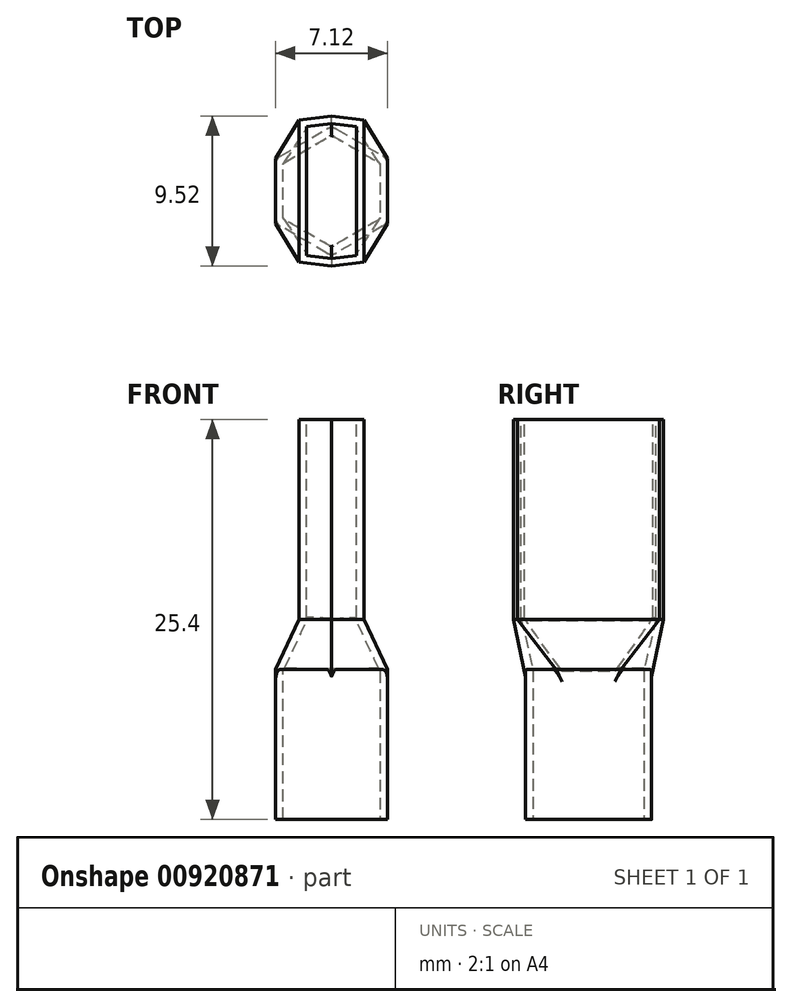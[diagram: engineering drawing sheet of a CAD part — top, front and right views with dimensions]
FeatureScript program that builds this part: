
annotation { "Feature Type Name" : "Feature", "Feature Type Description" : "" }
export const myFeature = defineFeature(function(context is Context, id is Id, definition is map)
    precondition{}
    {
        {
            var Q0;
            Q0=qCreatedBy(makeId("Top.planeOp"),FACE);
            var sketch = newSketch(context, id + "F0", { "sketchPlane" : qUnion([Q0])});
            skCircle(sketch, "E0.cCircle", {"center": v(0, 0) * mm, "radius": 3.56 * mm, "construction": true});
            skLineSegment(sketch, "E0.0", {"start": v(3.56, 2.05) * mm, "end": v(3.56, -2.05) * mm});
            skLineSegment(sketch, "E0.1", {"start": v(3.56, -2.05) * mm, "end": v(0, -4.1) * mm});
            skLineSegment(sketch, "E0.2", {"start": v(0, -4.1) * mm, "end": v(-3.56, -2.05) * mm});
            skLineSegment(sketch, "E0.3", {"start": v(-3.56, -2.05) * mm, "end": v(-3.56, 2.05) * mm});
            skLineSegment(sketch, "E0.4", {"start": v(-3.56, 2.05) * mm, "end": v(0, 4.1) * mm});
            skLineSegment(sketch, "E0.5", {"start": v(0, 4.1) * mm, "end": v(3.56, 2.05) * mm});
            skPoint(sketch, "E0.0.midPoint", {"position": v(3.56, 0) * mm});
            skSolve(sketch);
        }
        {
            var Q0;
            Q0=qSketchRegion(id+"F0",true);
            extrude(context, id + "F1", {"entities" : qUnion([Q0]), "depth" : 9.52 * mm, "offsetDistance" : 25.4 * mm});
        }
        {
            var Q0;
            Q0=makeQuery(id+"F1.opExtrude","CAP_FACE",FACE,{"disambiguationData":[OSD([sQuery(id+"F0.wireOp",EDGE,"E0.0"),sQuery(id+"F0.wireOp",EDGE,"E0.1"),sQuery(id+"F0.wireOp",EDGE,"E0.2"),sQuery(id+"F0.wireOp",EDGE,"E0.3"),sQuery(id+"F0.wireOp",EDGE,"E0.4"),sQuery(id+"F0.wireOp",EDGE,"E0.5")])],"isStart":false});
            cPlane(context, id + "F2", {"entities" : qUnion([Q0]), "cplaneType" : CPlaneType.OFFSET, "offset" : 15.88 * mm, "width" : 152.4 * mm, "height" : 152.4 * mm});
        }
        {
            var Q0;
            Q0=qCreatedBy(id+"F2.planeOp",FACE);
            var sketch = newSketch(context, id + "F3", { "sketchPlane" : qUnion([Q0])});
            skLineSegment(sketch, "E1.bottom", {"start": v(2.07, -4.5) * mm, "end": v(-2.07, -4.5) * mm, "construction": true});
            skLineSegment(sketch, "E1.top", {"start": v(2.07, 4.5) * mm, "end": v(-2.07, 4.5) * mm, "construction": true});
            skLineSegment(sketch, "E1.left", {"start": v(2.07, -4.5) * mm, "end": v(2.07, 4.5) * mm});
            skLineSegment(sketch, "E1.right", {"start": v(-2.07, -4.5) * mm, "end": v(-2.07, 4.5) * mm});
            skPoint(sketch, "E1.middle", {"position": v(0, 0) * mm});
            skLineSegment(sketch, "E2", {"start": v(-2.07, -4.5) * mm, "end": v(0, -4.76) * mm});
            skLineSegment(sketch, "E3", {"start": v(0, -4.76) * mm, "end": v(2.07, -4.5) * mm});
            skLineSegment(sketch, "E4", {"start": v(-2.07, 4.5) * mm, "end": v(0, 4.76) * mm});
            skLineSegment(sketch, "E5", {"start": v(0, 4.76) * mm, "end": v(2.07, 4.5) * mm});
            skSolve(sketch);
        }
        {
            var Q0;
            Q0=qSketchRegion(id+"F3",true);
            extrude(context, id + "F4", {"entities" : qUnion([Q0]), "oppositeDirection" : true, "depth" : 12.7 * mm, "offsetDistance" : 25.4 * mm});
        }
        {
            var Q0;
            Q0=makeQuery(id+"F1.opExtrude","CAP_FACE",FACE,{"disambiguationData":[OSD([sQuery(id+"F0.wireOp",EDGE,"E0.0"),sQuery(id+"F0.wireOp",EDGE,"E0.1"),sQuery(id+"F0.wireOp",EDGE,"E0.2"),sQuery(id+"F0.wireOp",EDGE,"E0.3"),sQuery(id+"F0.wireOp",EDGE,"E0.4"),sQuery(id+"F0.wireOp",EDGE,"E0.5")])],"isStart":false});
            var Q1;
            Q1=makeQuery(id+"F4.opExtrude","CAP_FACE",FACE,{"disambiguationData":[OSD([sQuery(id+"F3.wireOp",EDGE,"E1.left"),sQuery(id+"F3.wireOp",EDGE,"E1.right"),sQuery(id+"F3.wireOp",EDGE,"E2"),sQuery(id+"F3.wireOp",EDGE,"E3"),sQuery(id+"F3.wireOp",EDGE,"E4"),sQuery(id+"F3.wireOp",EDGE,"E5")])],"isStart":false});
            var Q2;
            Q2=makeQuery(id+"F4.opExtrude","CAP_FACE",FACE,{"disambiguationData":[OSD([sQuery(id+"F3.wireOp",EDGE,"E1.left"),sQuery(id+"F3.wireOp",EDGE,"E1.right"),sQuery(id+"F3.wireOp",EDGE,"E2"),sQuery(id+"F3.wireOp",EDGE,"E3"),sQuery(id+"F3.wireOp",EDGE,"E4"),sQuery(id+"F3.wireOp",EDGE,"E5")])],"isStart":false});
            var Q3;
            Q3=makeQuery(id+"F1.opExtrude","CAP_FACE",FACE,{"disambiguationData":[OSD([sQuery(id+"F0.wireOp",EDGE,"E0.0"),sQuery(id+"F0.wireOp",EDGE,"E0.1"),sQuery(id+"F0.wireOp",EDGE,"E0.2"),sQuery(id+"F0.wireOp",EDGE,"E0.3"),sQuery(id+"F0.wireOp",EDGE,"E0.4"),sQuery(id+"F0.wireOp",EDGE,"E0.5")])],"isStart":false});
            loft(context, id + "F5", {"operationType" : NewBodyOperationType.ADD, "sheetProfilesArray" : [{ "sheetProfileEntities" : qUnion([Q0]) }, { "sheetProfileEntities" : qUnion([Q1]) }], "wireProfilesArray" : [{ "wireProfileEntities" : qUnion([Q2]) }, { "wireProfileEntities" : qUnion([Q3]) }]});
        }
        {
            var Q0;
            Q0=makeQuery(id+"F1.opExtrude","SWEPT_EDGE",EDGE,{"disambiguationData":[OSD([sQuery(id+"F0.wireOp",EDGE,"E0.3"),sQuery(id+"F0.wireOp",EDGE,"E0.4")])]});
            var Q1;
            Q1=makeQuery(id+"F1.opExtrude","SWEPT_EDGE",EDGE,{"disambiguationData":[OSD([sQuery(id+"F0.wireOp",EDGE,"E0.2"),sQuery(id+"F0.wireOp",EDGE,"E0.3")])]});
            var Q2;
            Q2=makeQuery(id+"F1.opExtrude","SWEPT_EDGE",EDGE,{"disambiguationData":[OSD([sQuery(id+"F0.wireOp",EDGE,"E0.1"),sQuery(id+"F0.wireOp",EDGE,"E0.2")])]});
            var Q3;
            Q3=makeQuery(id+"F1.opExtrude","SWEPT_EDGE",EDGE,{"disambiguationData":[OSD([sQuery(id+"F0.wireOp",EDGE,"E0.0"),sQuery(id+"F0.wireOp",EDGE,"E0.1")])]});
            var Q4;
            Q4=makeQuery(id+"F1.opExtrude","SWEPT_EDGE",EDGE,{"disambiguationData":[OSD([sQuery(id+"F0.wireOp",EDGE,"E0.0"),sQuery(id+"F0.wireOp",EDGE,"E0.5")])]});
            var Q5;
            Q5=makeQuery(id+"F1.opExtrude","SWEPT_EDGE",EDGE,{"disambiguationData":[OSD([sQuery(id+"F0.wireOp",EDGE,"E0.4"),sQuery(id+"F0.wireOp",EDGE,"E0.5")])]});
            fillet(context, id + "F6", {"entities" : qUnion([Q0, Q1, Q2, Q3, Q4, Q5]), "radius" : 0.64 * mm, "tangentPropagation" : true, "allowEdgeOverflow" : false});
        }
        {
            var Q0;
            {var subQ0=sQuery(id+"F0.wireOp",EDGE,"E0.4");Q0=makeQuery(id+"FKWcXYWsRQ0RZtq_1.boolean.opBoolean","MERGE",FACE,{"derivedFrom":[makeQuery(id+"F1.opExtrude","CAP_FACE",FACE,{"disambiguationData":[OSD([sQuery(id+"F0.wireOp",EDGE,"E0.0"),sQuery(id+"F0.wireOp",EDGE,"E0.1"),sQuery(id+"F0.wireOp",EDGE,"E0.2"),sQuery(id+"F0.wireOp",EDGE,"E0.3"),subQ0,sQuery(id+"F0.wireOp",EDGE,"E0.5")])],"isStart":true}),makeQuery(id+"FKWcXYWsRQ0RZtq_1.opThicken","SWEPT_FACE",FACE,{"disambiguationData":[OSD([subQ0])]})]});}
            var Q1;
            {var subQ0=sQuery(id+"F3.wireOp",EDGE,"E1.right");Q1=makeQuery(id+"FKWcXYWsRQ0RZtq_1.boolean.opBoolean","MERGE",FACE,{"derivedFrom":[makeQuery(id+"F4.opExtrude","CAP_FACE",FACE,{"disambiguationData":[OSD([sQuery(id+"F3.wireOp",EDGE,"E1.left"),subQ0,sQuery(id+"F3.wireOp",EDGE,"E2"),sQuery(id+"F3.wireOp",EDGE,"E3"),sQuery(id+"F3.wireOp",EDGE,"E4"),sQuery(id+"F3.wireOp",EDGE,"E5")])],"isStart":true}),makeQuery(id+"FKWcXYWsRQ0RZtq_1.opThicken","SWEPT_FACE",FACE,{"disambiguationData":[OSD([subQ0])]})]});}
            shell(context, id + "F7", {"entities" : qUnion([Q0, Q1]), "thickness" : 0.48 * mm});
        }
    });
